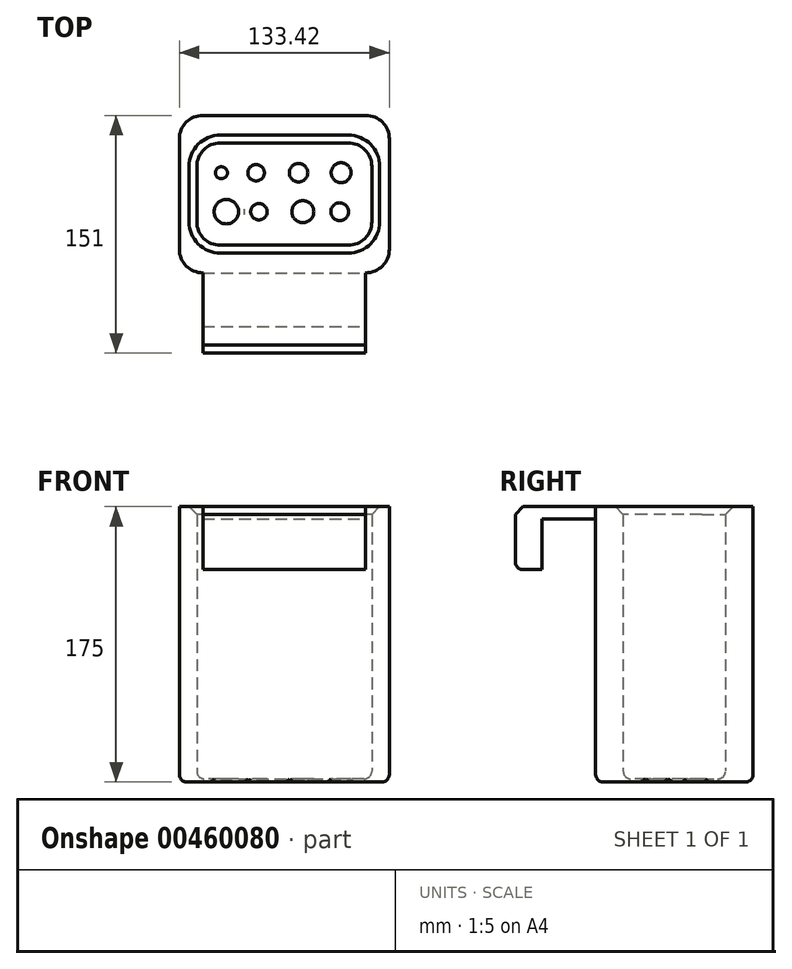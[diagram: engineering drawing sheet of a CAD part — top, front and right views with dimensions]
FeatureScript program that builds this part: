
annotation { "Feature Type Name" : "Feature", "Feature Type Description" : "" }
export const myFeature = defineFeature(function(context is Context, id is Id, definition is map)
    precondition{}
    {
        {
            var Q0;
            Q0=qCreatedBy(makeId("Top.planeOp"),FACE);
            var sketch = newSketch(context, id + "F0", { "sketchPlane" : qUnion([Q0])});
            skLineSegment(sketch, "E0.bottom", {"start": v(-66.7, 50) * mm, "end": v(66.7, 50) * mm});
            skLineSegment(sketch, "E0.top", {"start": v(-66.7, -50) * mm, "end": v(66.7, -50) * mm});
            skLineSegment(sketch, "E0.left", {"start": v(-66.7, 50) * mm, "end": v(-66.7, -50) * mm});
            skLineSegment(sketch, "E0.right", {"start": v(66.7, 50) * mm, "end": v(66.7, -50) * mm});
            skPoint(sketch, "E0.middle", {"position": v(0, 0) * mm});
            skLineSegment(sketch, "E1.bottom", {"start": v(-55.59, 32.5) * mm, "end": v(55.59, 32.5) * mm});
            skLineSegment(sketch, "E1.top", {"start": v(-55.59, -32.5) * mm, "end": v(55.59, -32.5) * mm});
            skLineSegment(sketch, "E1.left", {"start": v(-55.59, 32.5) * mm, "end": v(-55.59, -32.5) * mm});
            skLineSegment(sketch, "E1.right", {"start": v(55.59, 32.5) * mm, "end": v(55.59, -32.5) * mm});
            skSolve(sketch);
        }
        {
            var Q0;
            Q0=makeQuery(id+"F0.imprint","IMPRINT",FACE,{"disambiguationData":[TD([[makeQuery(id+"F0.imprint","IMPRINT",EDGE,{"derivedFrom":sQuery(id+"F0.wireOp",EDGE,"E0.bottom")}),-1.0]])]});
            extrude(context, id + "F1", {"entities" : qUnion([Q0]), "depth" : 175 * mm});
        }
        {
            var Q0;
            Q0=makeQuery(id+"F0.imprint","IMPRINT",FACE,{"disambiguationData":[TD([[makeQuery(id+"F0.imprint","IMPRINT",EDGE,{"derivedFrom":sQuery(id+"F0.wireOp",EDGE,"E1.bottom")}),-1.0]])]});
            extrude(context, id + "F2", {"entities" : qUnion([Q0]), "operationType" : NewBodyOperationType.ADD, "depth" : 2 * mm});
        }
        {
            var Q0;
            Q0=makeQuery(id+"F1.opExtrude","SWEPT_EDGE",EDGE,{"disambiguationData":[OSD([sQuery(id+"F0.wireOp",EDGE,"E0.top"),sQuery(id+"F0.wireOp",EDGE,"E0.right")])]});
            var Q1;
            Q1=makeQuery(id+"F1.opExtrude","SWEPT_EDGE",EDGE,{"disambiguationData":[OSD([sQuery(id+"F0.wireOp",EDGE,"E0.bottom"),sQuery(id+"F0.wireOp",EDGE,"E0.right")])]});
            var Q2;
            Q2=makeQuery(id+"F1.opExtrude","SWEPT_EDGE",EDGE,{"disambiguationData":[OSD([sQuery(id+"F0.wireOp",EDGE,"E0.top"),sQuery(id+"F0.wireOp",EDGE,"E0.left")])]});
            var Q3;
            Q3=makeQuery(id+"F1.opExtrude","SWEPT_EDGE",EDGE,{"disambiguationData":[OSD([sQuery(id+"F0.wireOp",EDGE,"E0.bottom"),sQuery(id+"F0.wireOp",EDGE,"E0.left")])]});
            var Q4;
            Q4=makeQuery(id+"F1.opExtrude","SWEPT_EDGE",EDGE,{"disambiguationData":[OSD([sQuery(id+"F0.wireOp",EDGE,"E1.top"),sQuery(id+"F0.wireOp",EDGE,"E1.right")])]});
            var Q5;
            Q5=makeQuery(id+"F1.opExtrude","SWEPT_EDGE",EDGE,{"disambiguationData":[OSD([sQuery(id+"F0.wireOp",EDGE,"E1.top"),sQuery(id+"F0.wireOp",EDGE,"E1.left")])]});
            var Q6;
            Q6=makeQuery(id+"F1.opExtrude","SWEPT_EDGE",EDGE,{"disambiguationData":[OSD([sQuery(id+"F0.wireOp",EDGE,"E1.bottom"),sQuery(id+"F0.wireOp",EDGE,"E1.left")])]});
            var Q7;
            Q7=makeQuery(id+"F1.opExtrude","SWEPT_EDGE",EDGE,{"disambiguationData":[OSD([sQuery(id+"F0.wireOp",EDGE,"E1.bottom"),sQuery(id+"F0.wireOp",EDGE,"E1.right")])]});
            fillet(context, id + "F3", {"entities" : qUnion([Q0, Q1, Q2, Q3, Q4, Q5, Q6, Q7]), "radius" : 15 * mm, "tangentPropagation" : true, "allowEdgeOverflow" : false});
        }
        {
            var Q0;
            Q0=makeQuery(id+"F1.opExtrude","CAP_FACE",FACE,{"disambiguationData":[OSD([sQuery(id+"F0.wireOp",EDGE,"E0.bottom"),sQuery(id+"F0.wireOp",EDGE,"E0.top"),sQuery(id+"F0.wireOp",EDGE,"E0.left"),sQuery(id+"F0.wireOp",EDGE,"E0.right"),sQuery(id+"F0.wireOp",EDGE,"E1.bottom"),sQuery(id+"F0.wireOp",EDGE,"E1.top"),sQuery(id+"F0.wireOp",EDGE,"E1.left"),sQuery(id+"F0.wireOp",EDGE,"E1.right")])],"isStart":false});
            var sketch = newSketch(context, id + "F4", { "sketchPlane" : qUnion([Q0])});
            skLineSegment(sketch, "E2.bottom", {"start": v(-51.7, -50) * mm, "end": v(51.7, -50) * mm});
            skLineSegment(sketch, "E2.top", {"start": v(-51.7, -84) * mm, "end": v(51.7, -84) * mm});
            skLineSegment(sketch, "E2.left", {"start": v(-51.7, -50) * mm, "end": v(-51.7, -84) * mm});
            skLineSegment(sketch, "E2.right", {"start": v(51.7, -50) * mm, "end": v(51.7, -84) * mm});
            skLineSegment(sketch, "E3.top", {"start": v(-51.7, -101) * mm, "end": v(51.7, -101) * mm});
            skLineSegment(sketch, "E3.left", {"start": v(-51.7, -50) * mm, "end": v(-51.7, -101) * mm});
            skLineSegment(sketch, "E3.right", {"start": v(51.7, -50) * mm, "end": v(51.7, -101) * mm});
            skSolve(sketch);
        }
        {
            var Q0;
            {var subQ0=sQuery(id+"F4.wireOp",EDGE,"E2.top");Q0=makeQuery(id+"F4.imprint","IMPRINT",FACE,{"disambiguationData":[TD([[makeQuery(id+"F4.imprint","IMPRINT",EDGE,{"derivedFrom":subQ0}),1.0]])]});}
            extrude(context, id + "F5", {"entities" : qUnion([Q0]), "operationType" : NewBodyOperationType.ADD, "oppositeDirection" : true, "depth" : 8 * mm});
        }
        {
            var Q0;
            {var subQ0=sQuery(id+"F4.wireOp",EDGE,"E2.top");Q0=makeQuery(id+"F4.imprint","IMPRINT",FACE,{"disambiguationData":[TD([[makeQuery(id+"F4.imprint","IMPRINT",EDGE,{"derivedFrom":subQ0}),-1.0]])]});}
            extrude(context, id + "F6", {"entities" : qUnion([Q0]), "operationType" : NewBodyOperationType.ADD, "oppositeDirection" : true, "depth" : 40 * mm});
        }
        {
            var Q0;
            Q0=makeQuery(id+"F6.opExtrude","CAP_EDGE",EDGE,{"disambiguationData":[OSD([sQuery(id+"F4.wireOp",EDGE,"E3.top")])],"isStart":true});
            var Q1;
            Q1=makeQuery(id+"F5.opExtrude","CAP_EDGE",EDGE,{"disambiguationData":[OSD([sQuery(id+"F4.wireOp",EDGE,"E2.top")])],"isStart":false});
            var Q2;
            Q2=makeQuery(id+"F5.opExtrude","CAP_EDGE",EDGE,{"disambiguationData":[OSD([sQuery(id+"F4.wireOp",EDGE,"E2.bottom")])],"isStart":false});
            chamfer(context, id + "F7", {"entities" : qUnion([Q0, Q1, Q2]), "width" : 5 * mm, "tangentPropagation" : true});
        }
        {
            var Q0;
            {var subQ0=sQuery(id+"F0.wireOp",EDGE,"E1.left");var subQ1=sQuery(id+"F0.wireOp",EDGE,"E1.top");Q0=makeQuery(id+"F3.opFillet","BLEND_EDGE",EDGE,{"blendedFrom":[makeQuery(id+"F1.opExtrude","SWEPT_EDGE",EDGE,{"disambiguationData":[OSD([subQ1,subQ0])]}),makeQuery(id+"F1.opExtrude","CAP_FACE",FACE,{"disambiguationData":[OSD([sQuery(id+"F0.wireOp",EDGE,"E0.bottom"),sQuery(id+"F0.wireOp",EDGE,"E0.top"),sQuery(id+"F0.wireOp",EDGE,"E0.left"),sQuery(id+"F0.wireOp",EDGE,"E0.right"),sQuery(id+"F0.wireOp",EDGE,"E1.bottom"),subQ1,subQ0,sQuery(id+"F0.wireOp",EDGE,"E1.right")])],"isStart":false})],"blendedInto":[makeQuery(id+"F1.opExtrude","CAP_FACE",FACE,{"disambiguationData":[OSD([sQuery(id+"F0.wireOp",EDGE,"E0.bottom"),sQuery(id+"F0.wireOp",EDGE,"E0.top"),sQuery(id+"F0.wireOp",EDGE,"E0.left"),sQuery(id+"F0.wireOp",EDGE,"E0.right"),sQuery(id+"F0.wireOp",EDGE,"E1.bottom"),subQ1,subQ0,sQuery(id+"F0.wireOp",EDGE,"E1.right")])],"isStart":false})]});}
            chamfer(context, id + "F8", {"entities" : qUnion([Q0]), "width" : 5 * mm, "tangentPropagation" : true});
        }
        {
            var Q0;
            Q0=makeQuery(id+"F2.opExtrude","CAP_FACE",FACE,{"disambiguationData":[OSD([sQuery(id+"F0.wireOp",EDGE,"E1.bottom"),sQuery(id+"F0.wireOp",EDGE,"E1.top"),sQuery(id+"F0.wireOp",EDGE,"E1.left"),sQuery(id+"F0.wireOp",EDGE,"E1.right")])],"isStart":false});
            fillet(context, id + "F9", {"entities" : qUnion([Q0]), "radius" : 5 * mm, "tangentPropagation" : true, "allowEdgeOverflow" : false});
        }
        {
            var Q0;
            Q0=makeQuery(id+"F6.opExtrude","CAP_EDGE",EDGE,{"disambiguationData":[OSD([sQuery(id+"F4.wireOp",EDGE,"E3.top")])],"isStart":false});
            fillet(context, id + "F10", {"entities" : qUnion([Q0]), "radius" : 5 * mm, "tangentPropagation" : true, "allowEdgeOverflow" : false});
        }
        {
            var Q0;
            Q0=qCreatedBy(makeId("Top.planeOp"),FACE);
            var sketch = newSketch(context, id + "F11", { "sketchPlane" : qUnion([Q0])});
            skCircle(sketch, "E4", {"center": v(-39.96, 13.57) * mm, "radius": 3.82 * mm});
            skCircle(sketch, "E5", {"center": v(-17.93, 13.57) * mm, "radius": 5.23 * mm});
            skCircle(sketch, "E6", {"center": v(9.05, 13.57) * mm, "radius": 5.86 * mm});
            skCircle(sketch, "E7", {"center": v(36.03, 13.57) * mm, "radius": 6.34 * mm});
            skCircle(sketch, "E8", {"center": v(35.13, -11.17) * mm, "radius": 5.64 * mm});
            skCircle(sketch, "E9", {"center": v(11.75, -11.17) * mm, "radius": 6.98 * mm});
            skCircle(sketch, "E10", {"center": v(-36.81, -11.17) * mm, "radius": 7.74 * mm});
            skCircle(sketch, "E11", {"center": v(-16.13, -11.17) * mm, "radius": 5.23 * mm});
            skLineSegment(sketch, "E12", {"start": v(-47.6, 13.57) * mm, "end": v(73.13, 13.57) * mm});
            skLineSegment(sketch, "E13", {"start": v(-51.88, -11.17) * mm, "end": v(50.87, -11.17) * mm});
            skSolve(sketch);
        }
        {
            var Q0;
            Q0=makeQuery(id+"F11.imprint","IMPRINT",FACE,{"disambiguationData":[TD([[makeQuery(id+"F11.imprint","IMPRINT",EDGE,{"derivedFrom":sQuery(id+"F11.wireOp",EDGE,"E9")}),1.0]])]});
            var Q1;
            Q1=makeQuery(id+"F11.imprint","IMPRINT",FACE,{"disambiguationData":[TD([[makeQuery(id+"F11.imprint","IMPRINT",EDGE,{"derivedFrom":sQuery(id+"F11.wireOp",EDGE,"E6")}),1.0]])]});
            var Q2;
            Q2=makeQuery(id+"F11.imprint","IMPRINT",FACE,{"disambiguationData":[TD([[makeQuery(id+"F11.imprint","IMPRINT",EDGE,{"derivedFrom":sQuery(id+"F11.wireOp",EDGE,"E7")}),1.0]])]});
            var Q3;
            Q3=makeQuery(id+"F11.imprint","IMPRINT",FACE,{"disambiguationData":[TD([[makeQuery(id+"F11.imprint","IMPRINT",EDGE,{"derivedFrom":sQuery(id+"F11.wireOp",EDGE,"E8")}),1.0]])]});
            var Q4;
            Q4=makeQuery(id+"F11.imprint","IMPRINT",FACE,{"disambiguationData":[TD([[makeQuery(id+"F11.imprint","IMPRINT",EDGE,{"derivedFrom":sQuery(id+"F11.wireOp",EDGE,"E10")}),1.0]])]});
            var Q5;
            Q5=makeQuery(id+"F11.imprint","IMPRINT",FACE,{"disambiguationData":[TD([[makeQuery(id+"F11.imprint","IMPRINT",EDGE,{"derivedFrom":sQuery(id+"F11.wireOp",EDGE,"E11")}),1.0]])]});
            var Q6;
            Q6=makeQuery(id+"F11.imprint","IMPRINT",FACE,{"disambiguationData":[TD([[makeQuery(id+"F11.imprint","IMPRINT",EDGE,{"derivedFrom":sQuery(id+"F11.wireOp",EDGE,"E5")}),1.0]])]});
            var Q7;
            Q7=makeQuery(id+"F11.imprint","IMPRINT",FACE,{"disambiguationData":[TD([[makeQuery(id+"F11.imprint","IMPRINT",EDGE,{"derivedFrom":sQuery(id+"F11.wireOp",EDGE,"E4")}),1.0]])]});
            extrude(context, id + "F12", {"entities" : qUnion([Q0, Q1, Q2, Q3, Q4, Q5, Q6, Q7]), "operationType" : NewBodyOperationType.REMOVE, "oppositeDirection" : true, "depth" : -25 * mm});
        }
        {
            var Q0;
            {var subQ0=sQuery(id+"F0.wireOp",EDGE,"E1.right");var subQ1=sQuery(id+"F0.wireOp",EDGE,"E1.left");var subQ2=sQuery(id+"F0.wireOp",EDGE,"E1.top");var subQ3=sQuery(id+"F0.wireOp",EDGE,"E1.bottom");Q0=makeQuery(id+"F2.boolean.opBoolean","MERGE",FACE,{"derivedFrom":[makeQuery(id+"F1.opExtrude","CAP_FACE",FACE,{"disambiguationData":[OSD([sQuery(id+"F0.wireOp",EDGE,"E0.bottom"),sQuery(id+"F0.wireOp",EDGE,"E0.top"),sQuery(id+"F0.wireOp",EDGE,"E0.left"),sQuery(id+"F0.wireOp",EDGE,"E0.right"),subQ3,subQ2,subQ1,subQ0])],"isStart":true}),makeQuery(id+"F2.opExtrude","CAP_FACE",FACE,{"disambiguationData":[OSD([subQ3,subQ2,subQ1,subQ0])],"isStart":true})]});}
            fillet(context, id + "F13", {"entities" : qUnion([Q0]), "radius" : 5 * mm, "tangentPropagation" : true, "allowEdgeOverflow" : false});
        }
    });
